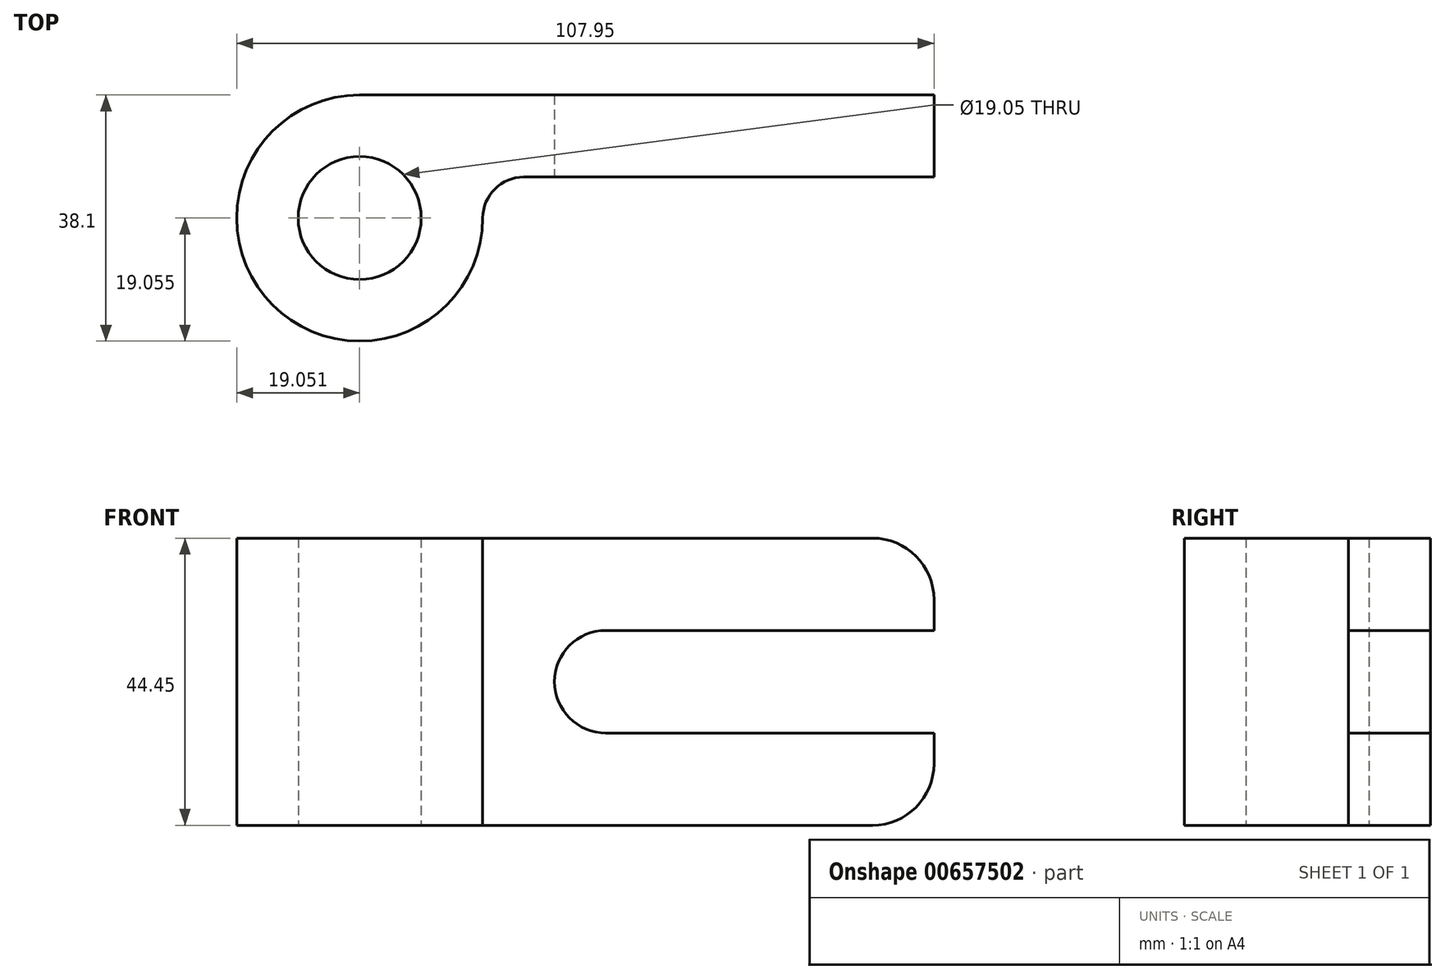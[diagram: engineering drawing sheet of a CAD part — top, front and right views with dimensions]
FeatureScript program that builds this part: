
annotation { "Feature Type Name" : "Feature", "Feature Type Description" : "" }
export const myFeature = defineFeature(function(context is Context, id is Id, definition is map)
    precondition{}
    {
        {
            var Q0;
            Q0=qCreatedBy(makeId("Top.planeOp"),FACE);
            var sketch = newSketch(context, id + "F0", { "sketchPlane" : qUnion([Q0])});
            skLineSegment(sketch, "E0.bottom", {"start": v(42.4, 4.15) * mm, "end": v(-46.5, 4.15) * mm});
            skLineSegment(sketch, "E0.top", {"start": v(42.4, -8.55) * mm, "end": v(-28.55, -8.55) * mm});
            skLineSegment(sketch, "E0.left", {"start": v(42.4, 4.15) * mm, "end": v(42.4, -8.55) * mm});
            skCircle(sketch, "E1", {"center": v(-46.5, -14.9) * mm, "radius": 19.05 * mm});
            skCircle(sketch, "E2", {"center": v(-46.5, -14.9) * mm, "radius": 9.53 * mm});
            skSolve(sketch);
        }
        {
            var Q0;
            Q0 = qSketchRegion(id + "F0", true);
            extrude(context, id + "F1", {"entities" : qUnion([Q0]), "depth" : 44.45 * mm, "offsetDistance" : 25.4 * mm});
        }
        {
            var Q0;
            Q0=makeQuery(id+"F1.opExtrude","CAP_EDGE",EDGE,{"disambiguationData":[OSD([sQuery(id+"F0.wireOp",EDGE,"E0.left")])],"isStart":false});
            var Q1;
            Q1=makeQuery(id+"F1.opExtrude","CAP_EDGE",EDGE,{"disambiguationData":[OSD([sQuery(id+"F0.wireOp",EDGE,"E0.left")])],"isStart":true});
            fillet(context, id + "F2", {"entities" : qUnion([Q0, Q1]), "radius" : 9.52 * mm, "tangentPropagation" : true, "allowEdgeOverflow" : false});
        }
        {
            var Q0;
            Q0=makeQuery(id+"F1.opExtrude","SWEPT_EDGE",EDGE,{"disambiguationData":[OSD([sQuery(id+"F0.wireOp",EDGE,"E0.top"),sQuery(id+"F0.wireOp",EDGE,"E1")])]});
            fillet(context, id + "F3", {"entities" : qUnion([Q0]), "radius" : 6.35 * mm, "tangentPropagation" : true, "allowEdgeOverflow" : false});
        }
        {
            var Q0;
            Q0=makeQuery(id+"F1.opExtrude","SWEPT_FACE",FACE,{"disambiguationData":[OSD([sQuery(id+"F0.wireOp",EDGE,"E0.top")])]});
            var sketch = newSketch(context, id + "F4", { "sketchPlane" : qUnion([Q0])});
            skLineSegment(sketch, "E3.bottom", {"start": v(42.4, 30.16) * mm, "end": v(-8.4, 30.16) * mm});
            skLineSegment(sketch, "E3.top", {"start": v(42.4, 14.29) * mm, "end": v(-8.4, 14.29) * mm});
            skLineSegment(sketch, "E3.left", {"start": v(42.4, 30.16) * mm, "end": v(42.4, 14.29) * mm});
            skArc(sketch, "E4", {"start": v(-8.4, 30.16) * mm, "mid": v(-16.35, 22.22) * mm, "end": v(-8.4, 14.29) * mm});
            skSolve(sketch);
        }
        {
            var Q0;
            Q0 = qSketchRegion(id + "F4", true);
            extrude(context, id + "F5", {"entities" : qUnion([Q0]), "operationType" : NewBodyOperationType.REMOVE, "endBound" : BoundingType.THROUGH_ALL, "oppositeDirection" : true, "depth" : 25.4 * mm, "offsetDistance" : 25.4 * mm});
        }
    });
